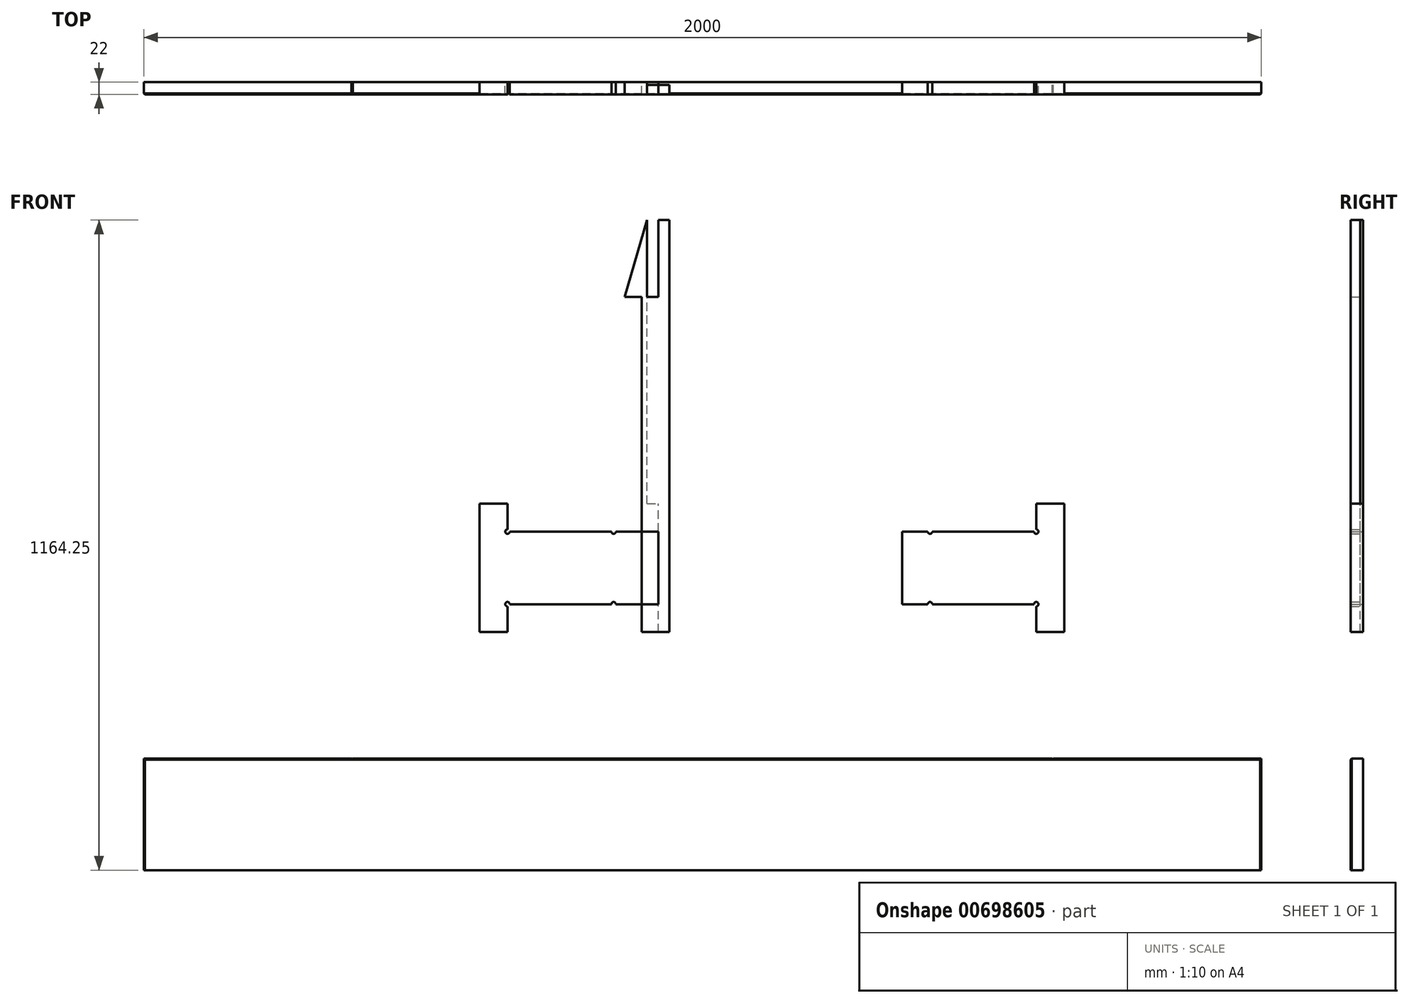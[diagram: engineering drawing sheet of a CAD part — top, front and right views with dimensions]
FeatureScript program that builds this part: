
annotation { "Feature Type Name" : "Feature", "Feature Type Description" : "" }
export const myFeature = defineFeature(function(context is Context, id is Id, definition is map)
    precondition{}
    {
        {
            var Q0;
            Q0=qCreatedBy(makeId("Front.planeOp"),FACE);
            var sketch = newSketch(context, id + "F0", { "sketchPlane" : qUnion([Q0])});
            skLineSegment(sketch, "E0.bottom", {"start": v(-273.1, -353.98) * mm, "end": v(66.9, -353.98) * mm});
            skLineSegment(sketch, "E0.top", {"start": v(-273.1, -123.98) * mm, "end": v(66.9, -123.98) * mm});
            skLineSegment(sketch, "E0.left", {"start": v(-273.1, -353.98) * mm, "end": v(-273.1, -123.98) * mm});
            skLineSegment(sketch, "E0.right", {"start": v(66.9, -353.98) * mm, "end": v(66.9, -123.98) * mm});
            skLineSegment(sketch, "E1.bottom", {"start": v(66.9, -353.98) * mm, "end": v(46.9, -353.98) * mm});
            skLineSegment(sketch, "E1.left", {"start": v(66.9, -353.98) * mm, "end": v(66.9, 384) * mm});
            skLineSegment(sketch, "E1.right", {"start": v(46.9, -353.98) * mm, "end": v(46.9, 384) * mm});
            skLineSegment(sketch, "E2.top", {"start": v(66.9, 246.02) * mm, "end": v(46.9, 246.02) * mm});
            skLineSegment(sketch, "E2.left", {"start": v(66.9, -353.98) * mm, "end": v(66.9, 246.02) * mm});
            skLineSegment(sketch, "E2.right", {"start": v(46.9, -353.98) * mm, "end": v(46.9, 246.02) * mm});
            skLineSegment(sketch, "E3.bottom", {"start": v(46.9, 246.02) * mm, "end": v(16.9, 246.02) * mm});
            skLineSegment(sketch, "E3.top", {"start": v(46.9, -353.98) * mm, "end": v(16.9, -353.98) * mm});
            skLineSegment(sketch, "E3.left", {"start": v(46.9, 246.02) * mm, "end": v(46.9, -353.98) * mm});
            skLineSegment(sketch, "E3.right", {"start": v(16.9, 246.02) * mm, "end": v(16.9, -353.98) * mm});
            skLineSegment(sketch, "E4", {"start": v(16.9, 246.02) * mm, "end": v(-13.1, 246.02) * mm});
            skLineSegment(sketch, "E5.top", {"start": v(66.9, -283.98) * mm, "end": v(46.9, -283.98) * mm});
            skLineSegment(sketch, "E5.left", {"start": v(66.9, -353.98) * mm, "end": v(66.9, -283.98) * mm});
            skLineSegment(sketch, "E5.right", {"start": v(46.9, -353.98) * mm, "end": v(46.9, -283.98) * mm});
            skLineSegment(sketch, "E6.bottom", {"start": v(-273.1, -353.98) * mm, "end": v(-223.1, -353.98) * mm});
            skLineSegment(sketch, "E6.top", {"start": v(-273.1, -303.98) * mm, "end": v(-223.1, -303.98) * mm});
            skLineSegment(sketch, "E6.left", {"start": v(-273.1, -353.98) * mm, "end": v(-273.1, -303.98) * mm});
            skLineSegment(sketch, "E6.right", {"start": v(-223.1, -353.98) * mm, "end": v(-223.1, -303.98) * mm});
            skLineSegment(sketch, "E7.bottom", {"start": v(-273.1, -123.98) * mm, "end": v(-223.1, -123.98) * mm});
            skLineSegment(sketch, "E7.top", {"start": v(-273.1, -173.98) * mm, "end": v(-223.1, -173.98) * mm});
            skLineSegment(sketch, "E7.left", {"start": v(-273.1, -123.98) * mm, "end": v(-273.1, -173.98) * mm});
            skLineSegment(sketch, "E7.right", {"start": v(-223.1, -123.98) * mm, "end": v(-223.1, -173.98) * mm});
            skLineSegment(sketch, "E8.bottom", {"start": v(66.9, -123.98) * mm, "end": v(16.9, -123.98) * mm});
            skLineSegment(sketch, "E8.top", {"start": v(66.9, -173.98) * mm, "end": v(16.9, -173.98) * mm});
            skLineSegment(sketch, "E8.left", {"start": v(66.9, -123.98) * mm, "end": v(66.9, -173.98) * mm});
            skLineSegment(sketch, "E8.right", {"start": v(16.9, -123.98) * mm, "end": v(16.9, -173.98) * mm});
            skLineSegment(sketch, "E9.bottom", {"start": v(66.9, -353.98) * mm, "end": v(16.9, -353.98) * mm});
            skLineSegment(sketch, "E9.top", {"start": v(66.9, -303.98) * mm, "end": v(16.9, -303.98) * mm});
            skLineSegment(sketch, "E9.left", {"start": v(66.9, -353.98) * mm, "end": v(66.9, -303.98) * mm});
            skLineSegment(sketch, "E9.right", {"start": v(16.9, -353.98) * mm, "end": v(16.9, -303.98) * mm});
            skLineSegment(sketch, "E10.bottom", {"start": v(-223.1, -173.98) * mm, "end": v(16.9, -173.98) * mm});
            skLineSegment(sketch, "E10.top", {"start": v(-223.1, -303.98) * mm, "end": v(16.9, -303.98) * mm});
            skLineSegment(sketch, "E10.left", {"start": v(-223.1, -173.98) * mm, "end": v(-223.1, -303.98) * mm});
            skLineSegment(sketch, "E10.right", {"start": v(16.9, -173.98) * mm, "end": v(16.9, -303.98) * mm});
            skPoint(sketch, "E11", {"position": v(-223.1, -173.98) * mm});
            skPoint(sketch, "E12", {"position": v(-223.1, -303.98) * mm});
            skPoint(sketch, "E13", {"position": v(56.9, 246.02) * mm});
            skLineSegment(sketch, "E14.top", {"start": v(66.9, 366.02) * mm, "end": v(46.9, 366.02) * mm});
            skLineSegment(sketch, "E14.left", {"start": v(66.9, 246.02) * mm, "end": v(66.9, 366.02) * mm});
            skLineSegment(sketch, "E14.right", {"start": v(46.9, 246.02) * mm, "end": v(46.9, 366.02) * mm});
            skPoint(sketch, "E15", {"position": v(56.9, 366.02) * mm});
            skLineSegment(sketch, "E16.top", {"start": v(66.9, 96.02) * mm, "end": v(46.9, 96.02) * mm});
            skLineSegment(sketch, "E16.left", {"start": v(66.9, 246.02) * mm, "end": v(66.9, 96.02) * mm});
            skLineSegment(sketch, "E16.right", {"start": v(46.9, 246.02) * mm, "end": v(46.9, 96.02) * mm});
            skLineSegment(sketch, "E17.bottom", {"start": v(46.9, 96.02) * mm, "end": v(66.9, 96.02) * mm});
            skLineSegment(sketch, "E17.top", {"start": v(46.9, -53.98) * mm, "end": v(66.9, -53.98) * mm});
            skLineSegment(sketch, "E17.left", {"start": v(46.9, 96.02) * mm, "end": v(46.9, -53.98) * mm});
            skLineSegment(sketch, "E17.right", {"start": v(66.9, 96.02) * mm, "end": v(66.9, -53.98) * mm});
            skPoint(sketch, "E18", {"position": v(56.9, 96.02) * mm});
            skPoint(sketch, "E19", {"position": v(56.9, -53.98) * mm});
            skLineSegment(sketch, "E20.bottom", {"start": v(66.9, -173.98) * mm, "end": v(-33.1, -173.98) * mm});
            skLineSegment(sketch, "E20.top", {"start": v(66.9, -303.98) * mm, "end": v(-33.1, -303.98) * mm});
            skLineSegment(sketch, "E20.left", {"start": v(66.9, -173.98) * mm, "end": v(66.9, -303.98) * mm});
            skLineSegment(sketch, "E20.right", {"start": v(-33.1, -173.98) * mm, "end": v(-33.1, -303.98) * mm});
            skPoint(sketch, "E21", {"position": v(-33.1, -173.98) * mm});
            skPoint(sketch, "E22", {"position": v(-33.1, -303.98) * mm});
            skLineSegment(sketch, "E23.bottom", {"start": v(66.9, -53.98) * mm, "end": v(46.9, -53.98) * mm});
            skLineSegment(sketch, "E23.top", {"start": v(66.9, -203.98) * mm, "end": v(46.9, -203.98) * mm});
            skLineSegment(sketch, "E23.left", {"start": v(66.9, -53.98) * mm, "end": v(66.9, -203.98) * mm});
            skLineSegment(sketch, "E23.right", {"start": v(46.9, -53.98) * mm, "end": v(46.9, -203.98) * mm});
            skPoint(sketch, "E24", {"position": v(56.9, -203.98) * mm});
            skLineSegment(sketch, "E25.bottom", {"start": v(66.9, -283.98) * mm, "end": v(26.9, -283.98) * mm});
            skLineSegment(sketch, "E25.left", {"start": v(66.9, -283.98) * mm, "end": v(66.9, 384) * mm});
            skLineSegment(sketch, "E25.right", {"start": v(26.9, -283.98) * mm, "end": v(26.9, 384) * mm});
            skLineSegment(sketch, "E26", {"start": v(26.9, 384) * mm, "end": v(66.9, 384) * mm});
            skLineSegment(sketch, "E27", {"start": v(26.9, 384) * mm, "end": v(-13.1, 246.02) * mm});
            skLineSegment(sketch, "E28", {"start": v(-13.1, 246.02) * mm, "end": v(66.1, 519.23) * mm, "construction": true});
            skLineSegment(sketch, "E29", {"start": v(66.1, 519.23) * mm, "end": v(168.51, 465.33) * mm, "construction": true});
            skLineSegment(sketch, "E30.bottom", {"start": v(66.9, 384) * mm, "end": v(31.9, 384) * mm, "construction": true});
            skLineSegment(sketch, "E30.top", {"start": v(66.9, 409) * mm, "end": v(31.9, 409) * mm, "construction": true});
            skLineSegment(sketch, "E30.left", {"start": v(66.9, 384) * mm, "end": v(66.9, 409) * mm, "construction": true});
            skLineSegment(sketch, "E30.right", {"start": v(31.9, 384) * mm, "end": v(31.9, 409) * mm, "construction": true});
            skPoint(sketch, "E31", {"position": v(34.14, 409) * mm});
            skSolve(sketch);
        }
        {
            var Q0;
            Q0=makeQuery(id+"F0.imprint","IMPRINT",FACE,{"disambiguationData":[TD([[makeQuery(id+"F0.imprint","IMPRINT",EDGE,{"derivedFrom":sQuery(id+"F0.wireOp",EDGE,"E0.top")}),-1.0]])]});
            var Q1;
            Q1=makeQuery(id+"F0.imprint","IMPRINT",FACE,{"disambiguationData":[TD([[makeQuery(id+"F0.imprint","IMPRINT",EDGE,{"derivedFrom":sQuery(id+"F0.wireOp",EDGE,"E1.right")}),1.0]])]});
            var Q2;
            {var subQ1=sQuery(id+"F0.wireOp",EDGE,"E3.left");Q2=makeQuery(id+"F0.imprint","IMPRINT",FACE,{"disambiguationData":[TD([[makeQuery(id+"F0.imprint","IMPRINT",EDGE,{"derivedFrom":subQ1}),-1.0]])]});}
            var Q3;
            {var subQ1=sQuery(id+"F0.wireOp",EDGE,"E16.right");Q3=makeQuery(id+"F0.imprint","IMPRINT",FACE,{"disambiguationData":[TD([[makeQuery(id+"F0.imprint","IMPRINT",EDGE,{"derivedFrom":subQ1}),-1.0]])]});}
            var Q4;
            {var subQ0=sQuery(id+"F0.wireOp",EDGE,"E23.right");var subQ1=sQuery(id+"F0.wireOp",EDGE,"E8.bottom");var subQ2=makeQuery(id+"F0.imprint","INTERSECT",VERTEX,{"derivedFrom":[subQ1,subQ0]});Q4=makeQuery(id+"F0.imprint","IMPRINT",FACE,{"disambiguationData":[TD([[makeQuery(id+"F0.imprint","IMPRINT",EDGE,{"disambiguationData":[TD([[subQ2,-1.0]])],"derivedFrom":subQ1}),1.0]])]});}
            var Q5;
            {var subQ0=sQuery(id+"F0.wireOp",EDGE,"E8.right");Q5=makeQuery(id+"F0.imprint","IMPRINT",FACE,{"disambiguationData":[TD([[makeQuery(id+"F0.imprint","IMPRINT",EDGE,{"derivedFrom":subQ0}),1.0]])]});}
            var Q6;
            {var subQ0=sQuery(id+"F0.wireOp",EDGE,"E2.top");Q6=makeQuery(id+"F0.imprint","IMPRINT",FACE,{"disambiguationData":[TD([[makeQuery(id+"F0.imprint","IMPRINT",EDGE,{"derivedFrom":subQ0}),1.0]])]});}
            var Q7;
            {var subQ5=sQuery(id+"F0.wireOp",EDGE,"E23.bottom");Q7=makeQuery(id+"F0.imprint","IMPRINT",FACE,{"disambiguationData":[TD([[makeQuery(id+"F0.imprint","IMPRINT",EDGE,{"derivedFrom":subQ5}),1.0]])]});}
            var Q8;
            {var subQ0=sQuery(id+"F0.wireOp",EDGE,"E17.bottom");Q8=makeQuery(id+"F0.imprint","IMPRINT",FACE,{"disambiguationData":[TD([[makeQuery(id+"F0.imprint","IMPRINT",EDGE,{"derivedFrom":subQ0}),-1.0]])]});}
            var Q9;
            {var subQ0=sQuery(id+"F0.wireOp",EDGE,"E14.top");Q9=makeQuery(id+"F0.imprint","IMPRINT",FACE,{"disambiguationData":[TD([[makeQuery(id+"F0.imprint","IMPRINT",EDGE,{"derivedFrom":subQ0}),1.0]])]});}
            var Q10;
            {var subQ0=sQuery(id+"F0.wireOp",EDGE,"E4");Q10=makeQuery(id+"F0.imprint","IMPRINT",FACE,{"disambiguationData":[TD([[makeQuery(id+"F0.imprint","IMPRINT",EDGE,{"derivedFrom":subQ0}),-1.0]])]});}
            var Q11;
            Q11=makeQuery(id+"F0.imprint","IMPRINT",FACE,{"disambiguationData":[TD([[makeQuery(id+"F0.imprint","IMPRINT",EDGE,{"derivedFrom":sQuery(id+"F0.wireOp",EDGE,"E6.bottom")}),1.0]])]});
            var Q12;
            Q12=makeQuery(id+"F0.imprint","IMPRINT",FACE,{"disambiguationData":[TD([[makeQuery(id+"F0.imprint","IMPRINT",EDGE,{"derivedFrom":sQuery(id+"F0.wireOp",EDGE,"E7.bottom")}),-1.0]])]});
            var Q13;
            {var subQ0=sQuery(id+"F0.wireOp",EDGE,"bba9a08c-ea9d-45fb-990c-955f8bffd41b.top");Q13=makeQuery(id+"F0.imprint","IMPRINT",FACE,{"disambiguationData":[TD([[makeQuery(id+"F0.imprint","IMPRINT",EDGE,{"derivedFrom":subQ0}),1.0]])]});}
            var Q14;
            Q14=makeQuery(id+"F0.imprint","IMPRINT",FACE,{"disambiguationData":[TD([[makeQuery(id+"F0.imprint","IMPRINT",EDGE,{"derivedFrom":sQuery(id+"F0.wireOp",EDGE,"E0.left")}),-1.0]])]});
            var Q15;
            Q15=makeQuery(id+"F0.imprint","IMPRINT",FACE,{"disambiguationData":[TD([[makeQuery(id+"F0.imprint","IMPRINT",EDGE,{"derivedFrom":sQuery(id+"F0.wireOp",EDGE,"E1.right")}),-1.0]])]});
            var Q16;
            {var subQ0=sQuery(id+"F0.wireOp",EDGE,"E3.right");Q16=makeQuery(id+"F0.imprint","IMPRINT",FACE,{"disambiguationData":[TD([[makeQuery(id+"F0.imprint","IMPRINT",EDGE,{"derivedFrom":subQ0}),1.0]])]});}
            var Q17;
            {var subQ0=sQuery(id+"F0.wireOp",EDGE,"E3.left");Q17=makeQuery(id+"F0.imprint","IMPRINT",FACE,{"disambiguationData":[TD([[makeQuery(id+"F0.imprint","IMPRINT",EDGE,{"derivedFrom":subQ0}),1.0]])]});}
            var Q18;
            {var subQ5=sQuery(id+"F0.wireOp",EDGE,"E9.right");Q18=makeQuery(id+"F0.imprint","IMPRINT",FACE,{"disambiguationData":[TD([[makeQuery(id+"F0.imprint","IMPRINT",EDGE,{"derivedFrom":subQ5}),-1.0]])]});}
            var Q19;
            {var subQ0=sQuery(id+"F0.wireOp",EDGE,"E25.left");var subQ1=sQuery(id+"F0.wireOp",EDGE,"E8.bottom");var subQ2=makeQuery(id+"F0.imprint","INTERSECT",VERTEX,{"derivedFrom":[subQ1,subQ0]});Q19=makeQuery(id+"F0.imprint","IMPRINT",FACE,{"disambiguationData":[TD([[makeQuery(id+"F0.imprint","IMPRINT",EDGE,{"disambiguationData":[TD([[subQ2,-1.0]])],"derivedFrom":subQ1}),1.0]])]});}
            var Q20;
            Q20=makeQuery(id+"F0.imprint","IMPRINT",FACE,{"disambiguationData":[TD([[makeQuery(id+"F0.imprint","IMPRINT",EDGE,{"derivedFrom":sQuery(id+"F0.wireOp",EDGE,"E10.bottom")}),-1.0]])]});
            var Q21;
            {var subQ0=sQuery(id+"F0.wireOp",EDGE,"E10.right");Q21=makeQuery(id+"F0.imprint","IMPRINT",FACE,{"disambiguationData":[TD([[makeQuery(id+"F0.imprint","IMPRINT",EDGE,{"derivedFrom":subQ0}),-1.0]])]});}
            var Q22;
            Q22=makeQuery(id+"F0.imprint","IMPRINT",FACE,{"disambiguationData":[TD([[makeQuery(id+"F0.imprint","IMPRINT",EDGE,{"derivedFrom":sQuery(id+"F0.wireOp",EDGE,"E0.bottom")}),1.0]])]});
            var Q23;
            {var subQ1=sQuery(id+"F0.wireOp",EDGE,"E10.right");Q23=makeQuery(id+"F0.imprint","IMPRINT",FACE,{"disambiguationData":[TD([[makeQuery(id+"F0.imprint","IMPRINT",EDGE,{"derivedFrom":subQ1}),1.0]])]});}
            var Q24;
            {var subQ5=sQuery(id+"F0.wireOp",EDGE,"E23.top");Q24=makeQuery(id+"F0.imprint","IMPRINT",FACE,{"disambiguationData":[TD([[makeQuery(id+"F0.imprint","IMPRINT",EDGE,{"derivedFrom":subQ5}),-1.0]])]});}
            extrude(context, id + "F1", {"entities" : qUnion([Q0, Q1, Q2, Q3, Q4, Q5, Q6, Q7, Q8, Q9, Q10, Q11, Q12, Q13, Q14, Q15, Q16, Q17, Q18, Q19, Q20, Q21, Q22, Q23, Q24]), "depth" : 22 * mm, "offsetDistance" : 25 * mm});
        }
        {
            var Q0;
            Q0=sQuery(id+"F0.wireOp",VERTEX,"bba9a08c-ea9d-45fb-990c-955f8bffd41b.left.end");
            var Q1;
            Q1=sQuery(id+"F0.wireOp",VERTEX,"E14.top.end");
            var Q2;
            Q2=sQuery(id+"F0.wireOp",VERTEX,"E3.bottom.start");
            var Q3;
            Q3=sQuery(id+"F0.wireOp",VERTEX,"E17.bottom.start");
            var Q4;
            Q4=sQuery(id+"F0.wireOp",VERTEX,"E23.right.start");
            var Q5;
            Q5=sQuery(id+"F0.wireOp",VERTEX,"E23.top.end");
            var Q6;
            Q6=sQuery(id+"F0.wireOp",VERTEX,"b3232fde-cd63-45e4-8105-18b5f4e3c0e731.MirrorCS.end");
            var Q7;
            Q7=sQuery(id+"F0.wireOp",VERTEX,"b3232fde-cd63-45e4-8105-18b5f4e3c0e745.MirrorCS.end");
            var Q8;
            Q8=sQuery(id+"F0.wireOp",VERTEX,"b3232fde-cd63-45e4-8105-18b5f4e3c0e75.MirrorCS.end");
            var Q9;
            Q9=sQuery(id+"F0.wireOp",VERTEX,"b3232fde-cd63-45e4-8105-18b5f4e3c0e713.MirrorCS.start");
            var Q10;
            Q10=sQuery(id+"F0.wireOp",VERTEX,"b3232fde-cd63-45e4-8105-18b5f4e3c0e79.MirrorCS.end");
            var Q11;
            Q11=sQuery(id+"F0.wireOp",VERTEX,"b3232fde-cd63-45e4-8105-18b5f4e3c0e728.MirrorCS.end");
            var Q12;
            Q12=makeQuery(id+"F1.opExtrude","SWEPT_BODY",BODY,{"disambiguationData":[OSD([sQuery(id+"F0.wireOp",EDGE,"E0.bottom"),sQuery(id+"F0.wireOp",EDGE,"E0.top"),sQuery(id+"F0.wireOp",EDGE,"E0.left"),sQuery(id+"F0.wireOp",EDGE,"E3.right"),sQuery(id+"F0.wireOp",EDGE,"E4"),sQuery(id+"F0.wireOp",EDGE,"9f31153a-71e7-4810-a313-33a1a7373bf2"),sQuery(id+"F0.wireOp",EDGE,"E5.right"),sQuery(id+"F0.wireOp",EDGE,"E6.bottom"),sQuery(id+"F0.wireOp",EDGE,"E6.left"),sQuery(id+"F0.wireOp",EDGE,"E7.bottom"),sQuery(id+"F0.wireOp",EDGE,"E7.left"),sQuery(id+"F0.wireOp",EDGE,"E9.bottom"),sQuery(id+"F0.wireOp",EDGE,"E25.bottom"),sQuery(id+"F0.wireOp",EDGE,"E25.top"),sQuery(id+"F0.wireOp",EDGE,"E25.left")])]});
            hole(context, id + "F2", {"style" : HoleStyle.SIMPLE, "endStyle" : HoleEndStyle.THROUGH, "oppositeDirection" : true, "holeDiameter" : 6 * mm, "majorDiameter" : 5 * mm, "isTappedThrough" : true, "tappedDepth" : 12 * mm, "tapClearance" : 3, "startFromSketch" : true, "locations" : qUnion([Q0, Q1, Q2, Q3, Q4, Q5, Q6, Q7, Q8, Q9, Q10, Q11]), "scope" : qUnion([Q12])});
        }
        {
            var Q0;
            Q0=sQuery(id+"F0.wireOp",VERTEX,"E21");
            var Q1;
            Q1=sQuery(id+"F0.wireOp",VERTEX,"E22");
            var Q2;
            Q2=sQuery(id+"F0.wireOp",VERTEX,"E12");
            var Q3;
            Q3=sQuery(id+"F0.wireOp",VERTEX,"E11");
            var Q4;
            Q4=sQuery(id+"F0.wireOp",VERTEX,"b3232fde-cd63-45e4-8105-18b5f4e3c0e779.MirrorP");
            var Q5;
            Q5=sQuery(id+"F0.wireOp",VERTEX,"b3232fde-cd63-45e4-8105-18b5f4e3c0e776.MirrorP");
            var Q6;
            Q6=sQuery(id+"F0.wireOp",VERTEX,"b3232fde-cd63-45e4-8105-18b5f4e3c0e780.MirrorP");
            var Q7;
            Q7=sQuery(id+"F0.wireOp",VERTEX,"b3232fde-cd63-45e4-8105-18b5f4e3c0e759.MirrorP");
            var Q8;
            Q8=makeQuery(id+"F1.opExtrude","SWEPT_BODY",BODY,{"disambiguationData":[OSD([sQuery(id+"F0.wireOp",EDGE,"E0.bottom"),sQuery(id+"F0.wireOp",EDGE,"E0.top"),sQuery(id+"F0.wireOp",EDGE,"E0.left"),sQuery(id+"F0.wireOp",EDGE,"E3.right"),sQuery(id+"F0.wireOp",EDGE,"E4"),sQuery(id+"F0.wireOp",EDGE,"9f31153a-71e7-4810-a313-33a1a7373bf2"),sQuery(id+"F0.wireOp",EDGE,"E5.right"),sQuery(id+"F0.wireOp",EDGE,"E6.bottom"),sQuery(id+"F0.wireOp",EDGE,"E6.left"),sQuery(id+"F0.wireOp",EDGE,"E7.bottom"),sQuery(id+"F0.wireOp",EDGE,"E7.left"),sQuery(id+"F0.wireOp",EDGE,"E9.bottom"),sQuery(id+"F0.wireOp",EDGE,"E25.bottom"),sQuery(id+"F0.wireOp",EDGE,"E25.top"),sQuery(id+"F0.wireOp",EDGE,"E25.left")])]});
            hole(context, id + "F3", {"style" : HoleStyle.SIMPLE, "endStyle" : HoleEndStyle.THROUGH, "oppositeDirection" : true, "holeDiameter" : 8 * mm, "majorDiameter" : 5 * mm, "isTappedThrough" : true, "tappedDepth" : 12 * mm, "tapClearance" : 3, "startFromSketch" : true, "locations" : qUnion([Q0, Q1, Q2, Q3, Q4, Q5, Q6, Q7]), "scope" : qUnion([Q8])});
        }
        {
            var Q0;
            {var subQ0=sQuery(id+"F0.wireOp",EDGE,"bba9a08c-ea9d-45fb-990c-955f8bffd41b.top");Q0=makeQuery(id+"F0.imprint","IMPRINT",FACE,{"disambiguationData":[TD([[makeQuery(id+"F0.imprint","IMPRINT",EDGE,{"derivedFrom":subQ0}),1.0]])]});}
            var Q1;
            Q1=makeQuery(id+"F0.imprint","IMPRINT",FACE,{"disambiguationData":[TD([[makeQuery(id+"F0.imprint","IMPRINT",EDGE,{"derivedFrom":sQuery(id+"F0.wireOp",EDGE,"E1.right")}),-1.0]])]});
            var Q2;
            Q2=makeQuery(id+"F0.imprint","IMPRINT",FACE,{"disambiguationData":[TD([[makeQuery(id+"F0.imprint","IMPRINT",EDGE,{"derivedFrom":sQuery(id+"F0.wireOp",EDGE,"E1.right")}),1.0]])]});
            var Q3;
            {var subQ0=sQuery(id+"F0.wireOp",EDGE,"E14.top");Q3=makeQuery(id+"F0.imprint","IMPRINT",FACE,{"disambiguationData":[TD([[makeQuery(id+"F0.imprint","IMPRINT",EDGE,{"derivedFrom":subQ0}),1.0]])]});}
            var Q4;
            {var subQ1=sQuery(id+"F0.wireOp",EDGE,"E16.right");Q4=makeQuery(id+"F0.imprint","IMPRINT",FACE,{"disambiguationData":[TD([[makeQuery(id+"F0.imprint","IMPRINT",EDGE,{"derivedFrom":subQ1}),-1.0]])]});}
            var Q5;
            {var subQ0=sQuery(id+"F0.wireOp",EDGE,"E2.top");Q5=makeQuery(id+"F0.imprint","IMPRINT",FACE,{"disambiguationData":[TD([[makeQuery(id+"F0.imprint","IMPRINT",EDGE,{"derivedFrom":subQ0}),1.0]])]});}
            var Q6;
            {var subQ0=sQuery(id+"F0.wireOp",EDGE,"E17.bottom");Q6=makeQuery(id+"F0.imprint","IMPRINT",FACE,{"disambiguationData":[TD([[makeQuery(id+"F0.imprint","IMPRINT",EDGE,{"derivedFrom":subQ0}),-1.0]])]});}
            var Q7;
            {var subQ5=sQuery(id+"F0.wireOp",EDGE,"E23.bottom");Q7=makeQuery(id+"F0.imprint","IMPRINT",FACE,{"disambiguationData":[TD([[makeQuery(id+"F0.imprint","IMPRINT",EDGE,{"derivedFrom":subQ5}),1.0]])]});}
            var Q8;
            {var subQ0=sQuery(id+"F0.wireOp",EDGE,"E25.left");var subQ1=sQuery(id+"F0.wireOp",EDGE,"E8.bottom");var subQ2=makeQuery(id+"F0.imprint","INTERSECT",VERTEX,{"derivedFrom":[subQ1,subQ0]});Q8=makeQuery(id+"F0.imprint","IMPRINT",FACE,{"disambiguationData":[TD([[makeQuery(id+"F0.imprint","IMPRINT",EDGE,{"disambiguationData":[TD([[subQ2,-1.0]])],"derivedFrom":subQ1}),1.0]])]});}
            var Q9;
            {var subQ5=sQuery(id+"F0.wireOp",EDGE,"E23.top");Q9=makeQuery(id+"F0.imprint","IMPRINT",FACE,{"disambiguationData":[TD([[makeQuery(id+"F0.imprint","IMPRINT",EDGE,{"derivedFrom":subQ5}),-1.0]])]});}
            var Q10;
            {var subQ0=sQuery(id+"F0.wireOp",EDGE,"E3.left");Q10=makeQuery(id+"F0.imprint","IMPRINT",FACE,{"disambiguationData":[TD([[makeQuery(id+"F0.imprint","IMPRINT",EDGE,{"derivedFrom":subQ0}),1.0]])]});}
            var Q11;
            {var subQ1=sQuery(id+"F0.wireOp",EDGE,"E3.left");Q11=makeQuery(id+"F0.imprint","IMPRINT",FACE,{"disambiguationData":[TD([[makeQuery(id+"F0.imprint","IMPRINT",EDGE,{"derivedFrom":subQ1}),-1.0]])]});}
            var Q12;
            {var subQ0=sQuery(id+"F0.wireOp",EDGE,"E23.right");var subQ1=sQuery(id+"F0.wireOp",EDGE,"E8.bottom");var subQ2=makeQuery(id+"F0.imprint","INTERSECT",VERTEX,{"derivedFrom":[subQ1,subQ0]});Q12=makeQuery(id+"F0.imprint","IMPRINT",FACE,{"disambiguationData":[TD([[makeQuery(id+"F0.imprint","IMPRINT",EDGE,{"disambiguationData":[TD([[subQ2,-1.0]])],"derivedFrom":subQ1}),1.0]])]});}
            var Q13;
            {var subQ5=sQuery(id+"F0.wireOp",EDGE,"b3232fde-cd63-45e4-8105-18b5f4e3c0e728.MirrorCS");Q13=makeQuery(id+"F0.imprint","IMPRINT",FACE,{"disambiguationData":[TD([[makeQuery(id+"F0.imprint","IMPRINT",EDGE,{"derivedFrom":subQ5}),-1.0]])]});}
            var Q14;
            {var subQ3=sQuery(id+"F0.wireOp",EDGE,"b3232fde-cd63-45e4-8105-18b5f4e3c0e777.MirrorCS");var subQ7=sQuery(id+"F0.wireOp",EDGE,"b3232fde-cd63-45e4-8105-18b5f4e3c0e719.MirrorCS");var subQ9=makeQuery(id+"F0.imprint","INTERSECT",VERTEX,{"derivedFrom":[subQ7,subQ3]});Q14=makeQuery(id+"F0.imprint","IMPRINT",FACE,{"disambiguationData":[TD([[makeQuery(id+"F0.imprint","IMPRINT",EDGE,{"disambiguationData":[TD([[subQ9,1.0]])],"derivedFrom":subQ7}),1.0]])]});}
            var Q15;
            {var subQ5=sQuery(id+"F0.wireOp",EDGE,"b3232fde-cd63-45e4-8105-18b5f4e3c0e728.MirrorCS");Q15=makeQuery(id+"F0.imprint","IMPRINT",FACE,{"disambiguationData":[TD([[makeQuery(id+"F0.imprint","IMPRINT",EDGE,{"derivedFrom":subQ5}),1.0]])]});}
            var Q16;
            {var subQ0=sQuery(id+"F0.wireOp",EDGE,"b3232fde-cd63-45e4-8105-18b5f4e3c0e774.MirrorCS");var subQ1=sQuery(id+"F0.wireOp",EDGE,"b3232fde-cd63-45e4-8105-18b5f4e3c0e724.MirrorCS");var subQ2=makeQuery(id+"F0.imprint","INTERSECT",VERTEX,{"derivedFrom":[subQ1,subQ0]});Q16=makeQuery(id+"F0.imprint","IMPRINT",FACE,{"disambiguationData":[TD([[makeQuery(id+"F0.imprint","IMPRINT",EDGE,{"disambiguationData":[TD([[subQ2,-1.0]])],"derivedFrom":subQ1}),1.0]])]});}
            var Q17;
            {var subQ0=sQuery(id+"F0.wireOp",EDGE,"b3232fde-cd63-45e4-8105-18b5f4e3c0e766.MirrorCS");var subQ1=sQuery(id+"F0.wireOp",EDGE,"b3232fde-cd63-45e4-8105-18b5f4e3c0e724.MirrorCS");var subQ2=makeQuery(id+"F0.imprint","INTERSECT",VERTEX,{"derivedFrom":[subQ1,subQ0]});Q17=makeQuery(id+"F0.imprint","IMPRINT",FACE,{"disambiguationData":[TD([[makeQuery(id+"F0.imprint","IMPRINT",EDGE,{"disambiguationData":[TD([[subQ2,-1.0]])],"derivedFrom":subQ1}),1.0]])]});}
            var Q18;
            {var subQ0=sQuery(id+"F0.wireOp",EDGE,"b3232fde-cd63-45e4-8105-18b5f4e3c0e767.MirrorCS");Q18=makeQuery(id+"F0.imprint","IMPRINT",FACE,{"disambiguationData":[TD([[makeQuery(id+"F0.imprint","IMPRINT",EDGE,{"derivedFrom":subQ0}),1.0]])]});}
            var Q19;
            {var subQ0=sQuery(id+"F0.wireOp",EDGE,"b3232fde-cd63-45e4-8105-18b5f4e3c0e711.MirrorCS");Q19=makeQuery(id+"F0.imprint","IMPRINT",FACE,{"disambiguationData":[TD([[makeQuery(id+"F0.imprint","IMPRINT",EDGE,{"derivedFrom":subQ0}),1.0]])]});}
            var Q20;
            {var subQ0=sQuery(id+"F0.wireOp",EDGE,"b3232fde-cd63-45e4-8105-18b5f4e3c0e711.MirrorCS");Q20=makeQuery(id+"F0.imprint","IMPRINT",FACE,{"disambiguationData":[TD([[makeQuery(id+"F0.imprint","IMPRINT",EDGE,{"derivedFrom":subQ0}),-1.0]])]});}
            var Q21;
            {var subQ0=sQuery(id+"F0.wireOp",EDGE,"b3232fde-cd63-45e4-8105-18b5f4e3c0e75.MirrorCS");Q21=makeQuery(id+"F0.imprint","IMPRINT",FACE,{"disambiguationData":[TD([[makeQuery(id+"F0.imprint","IMPRINT",EDGE,{"derivedFrom":subQ0}),-1.0]])]});}
            var Q22;
            {var subQ0=sQuery(id+"F0.wireOp",EDGE,"b3232fde-cd63-45e4-8105-18b5f4e3c0e757.MirrorCS");var subQ1=makeQuery(id+"F0.imprint","INTERSECT",VERTEX,{"derivedFrom":[sQuery(id+"F0.wireOp",EDGE,"b3232fde-cd63-45e4-8105-18b5f4e3c0e727.MirrorCS"),subQ0]});Q22=makeQuery(id+"F0.imprint","IMPRINT",FACE,{"disambiguationData":[TD([[makeQuery(id+"F0.imprint","IMPRINT",EDGE,{"disambiguationData":[TD([[subQ1,1.0]])],"derivedFrom":subQ0}),-1.0]])]});}
            var Q23;
            {var subQ0=sQuery(id+"F0.wireOp",EDGE,"b3232fde-cd63-45e4-8105-18b5f4e3c0e75.MirrorCS");Q23=makeQuery(id+"F0.imprint","IMPRINT",FACE,{"disambiguationData":[TD([[makeQuery(id+"F0.imprint","IMPRINT",EDGE,{"derivedFrom":subQ0}),1.0]])]});}
            var Q24;
            {var subQ0=sQuery(id+"F0.wireOp",EDGE,"b3232fde-cd63-45e4-8105-18b5f4e3c0e727.MirrorCS");Q24=makeQuery(id+"F0.imprint","IMPRINT",FACE,{"disambiguationData":[TD([[makeQuery(id+"F0.imprint","IMPRINT",EDGE,{"derivedFrom":subQ0}),1.0]])]});}
            var Q25;
            {var subQ5=sQuery(id+"F0.wireOp",EDGE,"b3232fde-cd63-45e4-8105-18b5f4e3c0e727.MirrorCS");Q25=makeQuery(id+"F0.imprint","IMPRINT",FACE,{"disambiguationData":[TD([[makeQuery(id+"F0.imprint","IMPRINT",EDGE,{"derivedFrom":subQ5}),-1.0]])]});}
            extrude(context, id + "F4", {"entities" : qUnion([Q0, Q1, Q2, Q3, Q4, Q5, Q6, Q7, Q8, Q9, Q10, Q11, Q12, Q13, Q14, Q15, Q16, Q17, Q18, Q19, Q20, Q21, Q22, Q23, Q24, Q25]), "operationType" : NewBodyOperationType.REMOVE, "depth" : 5 * mm, "offsetDistance" : 25 * mm});
        }
        {
            var Q0;
            Q0=qCreatedBy(makeId("Front.planeOp"),FACE);
            var sketch = newSketch(context, id + "F5", { "sketchPlane" : qUnion([Q0])});
            skLineSegment(sketch, "E32.bottom", {"start": v(-874.08, -580.24) * mm, "end": v(1125.92, -580.24) * mm});
            skLineSegment(sketch, "E32.top", {"start": v(-874.08, -780.24) * mm, "end": v(1125.92, -780.24) * mm});
            skLineSegment(sketch, "E32.left", {"start": v(-874.08, -580.24) * mm, "end": v(-874.08, -780.24) * mm});
            skLineSegment(sketch, "E32.right", {"start": v(1125.92, -580.24) * mm, "end": v(1125.92, -780.24) * mm});
            skPoint(sketch, "E33", {"position": v(-874.08, -680.24) * mm});
            skPoint(sketch, "E34", {"position": v(1125.92, -680.24) * mm});
            skLineSegment(sketch, "E35", {"start": v(-874.08, -680.24) * mm, "end": v(1125.92, -680.24) * mm, "construction": true});
            skLineSegment(sketch, "E36.top", {"start": v(-874.08, -780.24) * mm, "end": v(-501.08, -780.24) * mm, "construction": true});
            skLineSegment(sketch, "E36.left", {"start": v(-874.08, -580.24) * mm, "end": v(-874.08, -780.24) * mm, "construction": true});
            skLineSegment(sketch, "E36.right", {"start": v(-501.08, -580.24) * mm, "end": v(-501.08, -780.24) * mm, "construction": true});
            skLineSegment(sketch, "E37.bottom", {"start": v(1125.92, -580.24) * mm, "end": v(752.92, -580.24) * mm, "construction": true});
            skLineSegment(sketch, "E37.top", {"start": v(1125.92, -780.24) * mm, "end": v(752.92, -780.24) * mm, "construction": true});
            skLineSegment(sketch, "E37.left", {"start": v(1125.92, -580.24) * mm, "end": v(1125.92, -780.24) * mm, "construction": true});
            skLineSegment(sketch, "E37.right", {"start": v(752.92, -580.24) * mm, "end": v(752.92, -780.24) * mm, "construction": true});
            skLineSegment(sketch, "E38.bottom", {"start": v(-501.08, -580.24) * mm, "end": v(-601.6, -580.24) * mm});
            skLineSegment(sketch, "E38.left", {"start": v(-501.08, -580.24) * mm, "end": v(-501.08, -657.74) * mm});
            skLineSegment(sketch, "E39.bottom", {"start": v(752.92, -580.24) * mm, "end": v(872.76, -580.24) * mm});
            skLineSegment(sketch, "E39.left", {"start": v(752.92, -580.24) * mm, "end": v(752.92, -657.74) * mm});
            skLineSegment(sketch, "E40.top", {"start": v(752.92, -780.24) * mm, "end": v(-501.08, -780.24) * mm});
            skLineSegment(sketch, "E40.left", {"start": v(752.92, -657.74) * mm, "end": v(752.92, -780.24) * mm});
            skLineSegment(sketch, "E40.right", {"start": v(-501.08, -657.74) * mm, "end": v(-501.08, -780.24) * mm});
            skPoint(sketch, "E41", {"position": v(-501.08, -580.24) * mm});
            skPoint(sketch, "E42", {"position": v(752.92, -580.24) * mm});
            skSolve(sketch);
        }
        {
            var Q0;
            Q0 = qSketchRegion(id + "F5", true);
            extrude(context, id + "F6", {"entities" : qUnion([Q0]), "depth" : 22 * mm, "offsetDistance" : 25 * mm});
        }
        {
            var Q0;
            Q0=makeQuery(id+"F6.opExtrude","CAP_EDGE",EDGE,{"disambiguationData":[OSD([sQuery(id+"F5.wireOp",EDGE,"E32.bottom")])],"isStart":false});
            var Q1;
            Q1=makeQuery(id+"F6.opExtrude","CAP_EDGE",EDGE,{"disambiguationData":[OSD([sQuery(id+"F5.wireOp",EDGE,"E32.right")])],"isStart":false});
            var Q2;
            Q2=makeQuery(id+"F6.opExtrude","CAP_EDGE",EDGE,{"disambiguationData":[OSD([sQuery(id+"F5.wireOp",EDGE,"E32.left")])],"isStart":false});
            chamfer(context, id + "F7", {"entities" : qUnion([Q0, Q1, Q2]), "width" : 2 * mm, "tangentPropagation" : true});
        }
        {
            var Q0;
            Q0=qCreatedBy(makeId("Right.planeOp"),FACE);
            cPlane(context, id + "F8", {"entities" : qUnion([Q0]), "cplaneType" : CPlaneType.OFFSET, "offset" : 250 * mm, "width" : 150 * mm, "height" : 150 * mm});
        }
        {
            var Q0;
            Q0=makeQuery(id+"F1.opExtrude","SWEPT_FACE",FACE,{"disambiguationData":[OSD([sQuery(id+"F0.wireOp",EDGE,"E26")])]});
            var sketch = newSketch(context, id + "F9", { "sketchPlane" : qUnion([Q0])});
            skLineSegment(sketch, "E43", {"start": v(66.9, -22) * mm, "end": v(49.4, -22) * mm, "construction": true});
            skLineSegment(sketch, "E44", {"start": v(49.4, -22) * mm, "end": v(49.4, -11) * mm, "construction": true});
            skPoint(sketch, "E45", {"position": v(49.4, -11) * mm});
            skSolve(sketch);
        }
        {
            var Q0;
            Q0=sQuery(id+"F9.wireOp",VERTEX,"E45");
            var Q1;
            Q1=makeQuery(id+"F1.opExtrude","SWEPT_BODY",BODY,{"disambiguationData":[OSD([sQuery(id+"F0.wireOp",EDGE,"E0.bottom"),sQuery(id+"F0.wireOp",EDGE,"E0.top"),sQuery(id+"F0.wireOp",EDGE,"E0.left"),sQuery(id+"F0.wireOp",EDGE,"E3.right"),sQuery(id+"F0.wireOp",EDGE,"E4"),sQuery(id+"F0.wireOp",EDGE,"E5.right"),sQuery(id+"F0.wireOp",EDGE,"E6.bottom"),sQuery(id+"F0.wireOp",EDGE,"E6.left"),sQuery(id+"F0.wireOp",EDGE,"E7.bottom"),sQuery(id+"F0.wireOp",EDGE,"E7.left"),sQuery(id+"F0.wireOp",EDGE,"E9.bottom"),sQuery(id+"F0.wireOp",EDGE,"E25.bottom"),sQuery(id+"F0.wireOp",EDGE,"E25.left"),sQuery(id+"F0.wireOp",EDGE,"E26"),sQuery(id+"F0.wireOp",EDGE,"E27")])]});
            hole(context, id + "F10", {"style" : HoleStyle.SIMPLE, "endStyle" : HoleEndStyle.BLIND, "holeDiameter" : 2 * mm, "majorDiameter" : 5 * mm, "holeDepth" : 12 * mm, "isTappedThrough" : true, "tappedDepth" : 12 * mm, "tapClearance" : 3, "startFromSketch" : true, "locations" : qUnion([Q0]), "scope" : qUnion([Q1])});
        }
        {
            var Q0;
            Q0=makeQuery(id+"F1.opExtrude","SWEPT_BODY",BODY,{"disambiguationData":[OSD([sQuery(id+"F0.wireOp",EDGE,"E0.bottom"),sQuery(id+"F0.wireOp",EDGE,"E0.top"),sQuery(id+"F0.wireOp",EDGE,"E0.left"),sQuery(id+"F0.wireOp",EDGE,"E3.right"),sQuery(id+"F0.wireOp",EDGE,"E4"),sQuery(id+"F0.wireOp",EDGE,"E5.right"),sQuery(id+"F0.wireOp",EDGE,"E6.bottom"),sQuery(id+"F0.wireOp",EDGE,"E6.left"),sQuery(id+"F0.wireOp",EDGE,"E7.bottom"),sQuery(id+"F0.wireOp",EDGE,"E7.left"),sQuery(id+"F0.wireOp",EDGE,"E9.bottom"),sQuery(id+"F0.wireOp",EDGE,"E25.bottom"),sQuery(id+"F0.wireOp",EDGE,"E25.left"),sQuery(id+"F0.wireOp",EDGE,"E26"),sQuery(id+"F0.wireOp",EDGE,"E27")])]});
            var Q1;
            Q1=qCreatedBy(id+"F8.planeOp",FACE);
            mirror(context, id + "F11", {"entities" : qUnion([Q0]), "mirrorPlane" : qUnion([Q1])});
        }
        {
            var Q0;
            Q0=sQuery(id+"F5.wireOp",VERTEX,"E41");
            var Q1;
            Q1=sQuery(id+"F5.wireOp",VERTEX,"E42");
            var Q2;
            Q2=makeQuery(id+"F6.opExtrude","SWEPT_BODY",BODY,{"disambiguationData":[OSD([sQuery(id+"F5.wireOp",EDGE,"E32.bottom"),sQuery(id+"F5.wireOp",EDGE,"E32.top"),sQuery(id+"F5.wireOp",EDGE,"E32.left"),sQuery(id+"F5.wireOp",EDGE,"E32.right"),sQuery(id+"F5.wireOp",EDGE,"E38.bottom"),sQuery(id+"F5.wireOp",EDGE,"E39.bottom"),sQuery(id+"F5.wireOp",EDGE,"E40.top")])]});
            hole(context, id + "F12", {"style" : HoleStyle.SIMPLE, "endStyle" : HoleEndStyle.THROUGH, "oppositeDirection" : true, "holeDiameter" : 2 * mm, "majorDiameter" : 5 * mm, "isTappedThrough" : true, "tappedDepth" : 12 * mm, "tapClearance" : 3, "startFromSketch" : true, "locations" : qUnion([Q0, Q1]), "scope" : qUnion([Q2])});
        }
    });
